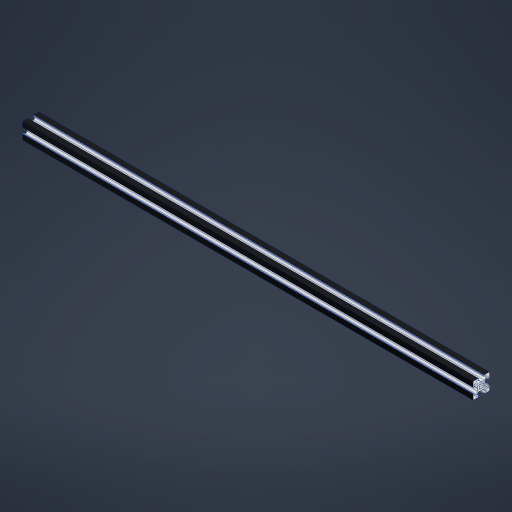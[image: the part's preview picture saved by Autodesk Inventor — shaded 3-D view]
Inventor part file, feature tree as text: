
AUTODESK INVENTOR PART (.ipt)
format: ipt  version: 2024.2 (Build 282272000, 272)  size: 329,728 bytes
history: native  units: mm
features: extrude x1, sketch x1
ambient origin geometry x8: Origin, YZ Plane, XZ Plane, XY Plane, X Axis, Y Axis, Z Axis, Center Point
bodies: Solid1 (feature_tree)
feature tree (2):
  extrude  "Extrusion1"  Depth=0.5mm
  sketch  "Sketch1"  dims[d2=6.5mm d3=0.5mm d4=4.0mm d5=3.465mm d6=5.48mm d7=0.795mm d8=0.305mm d9=2.95mm d11=0.75mm d14=45.0deg d15=10.0mm d16=1.0mm d17=3.0mm d18=45.0deg d19=40.0mm d21=360.0deg d23=550.0mm d24=0.0mm]
